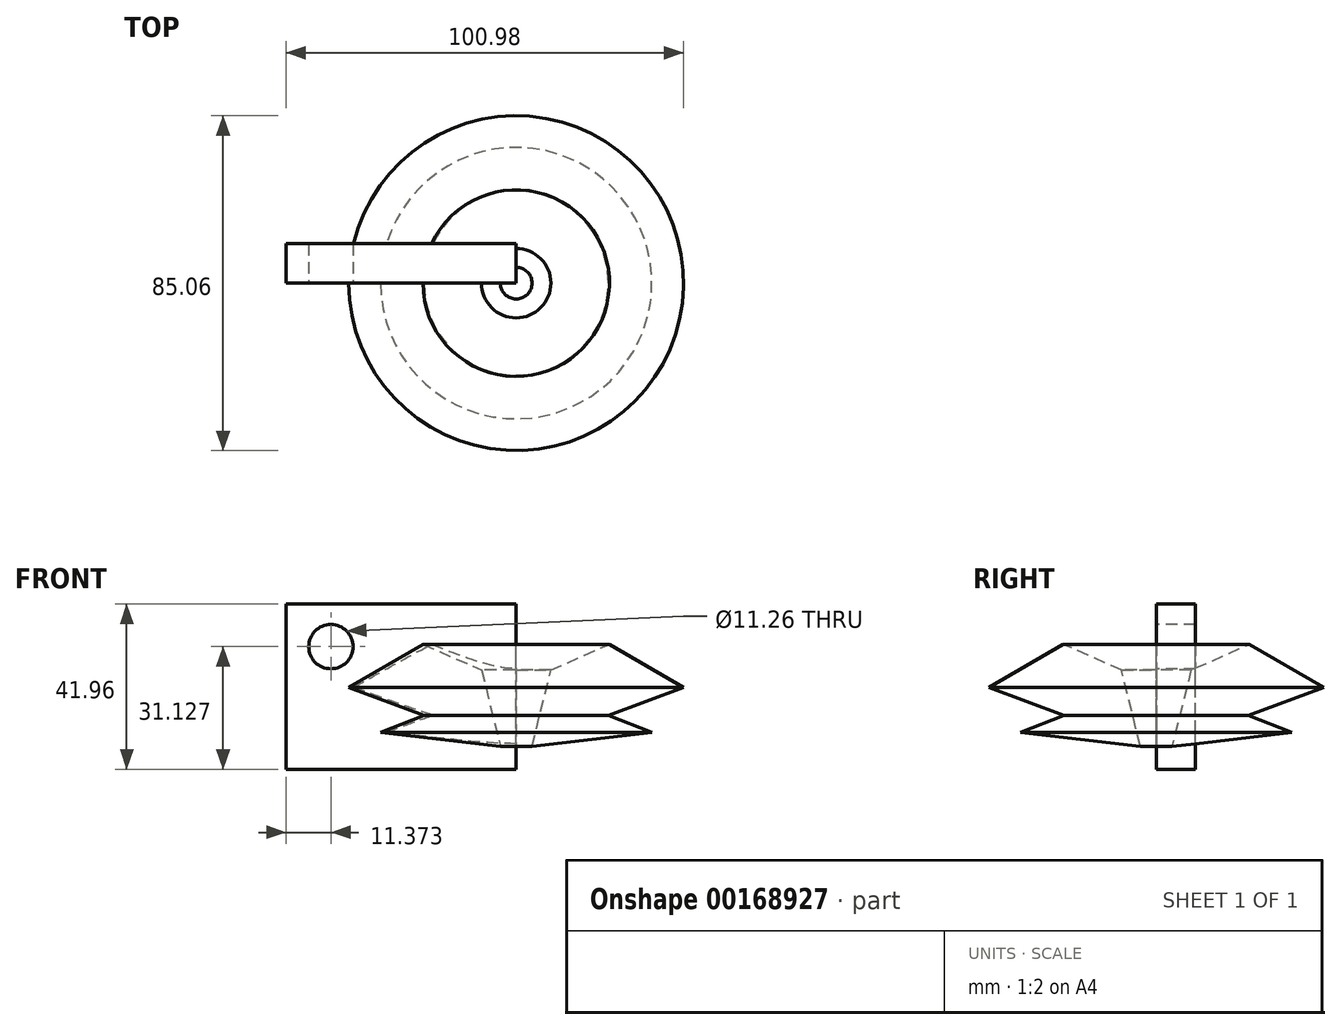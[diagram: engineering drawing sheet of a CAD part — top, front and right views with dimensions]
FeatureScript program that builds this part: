
annotation { "Feature Type Name" : "Feature", "Feature Type Description" : "" }
export const myFeature = defineFeature(function(context is Context, id is Id, definition is map)
    precondition{}
    {
        {
            var Q0;
            Q0=qCreatedBy(makeId("Front.planeOp"),FACE);
            var sketch = newSketch(context, id + "F0", { "sketchPlane" : qUnion([Q0])});
            skLineSegment(sketch, "E0.bottom", {"start": v(0, 0) * mm, "end": v(58.45, 0) * mm});
            skLineSegment(sketch, "E0.top", {"start": v(0, 41.96) * mm, "end": v(58.45, 41.96) * mm});
            skLineSegment(sketch, "E0.left", {"start": v(0, 0) * mm, "end": v(0, 41.96) * mm});
            skLineSegment(sketch, "E0.right", {"start": v(58.45, 0) * mm, "end": v(58.45, 41.96) * mm});
            skSolve(sketch);
        }
        {
            var Q0;
            Q0=makeQuery(id+"F0.imprint","IMPRINT",FACE,{"disambiguationData":[TD([[makeQuery(id+"F0.imprint","IMPRINT",EDGE,{"derivedFrom":sQuery(id+"F0.wireOp",EDGE,"E0.bottom")}),1.0]])]});
            extrude(context, id + "F1", {"entities" : qUnion([Q0]), "depth" : 10 * mm, "offsetDistance" : 25.4 * mm});
        }
        {
            var Q0;
            Q0=makeQuery(id+"F1.opExtrude","CAP_FACE",FACE,{"disambiguationData":[OSD([sQuery(id+"F0.wireOp",EDGE,"E0.bottom"),sQuery(id+"F0.wireOp",EDGE,"E0.top"),sQuery(id+"F0.wireOp",EDGE,"E0.left"),sQuery(id+"F0.wireOp",EDGE,"E0.right")])],"isStart":false});
            var sketch = newSketch(context, id + "F2", { "sketchPlane" : qUnion([Q0])});
            skCircle(sketch, "E1", {"center": v(11.37, 31.13) * mm, "radius": 5.63 * mm});
            skSolve(sketch);
        }
        {
            var Q0;
            Q0=makeQuery(id+"F2.imprint","IMPRINT",FACE,{"disambiguationData":[TD([[makeQuery(id+"F2.imprint","IMPRINT",EDGE,{"derivedFrom":sQuery(id+"F2.wireOp",EDGE,"E1")}),1.0]])]});
            extrude(context, id + "F3", {"entities" : qUnion([Q0]), "operationType" : NewBodyOperationType.REMOVE, "endBound" : BoundingType.THROUGH_ALL, "oppositeDirection" : true, "depth" : 25.4 * mm, "offsetDistance" : 25.4 * mm});
        }
        {
            var Q0;
            Q0=makeQuery(id+"F1.opExtrude","CAP_FACE",FACE,{"disambiguationData":[OSD([sQuery(id+"F0.wireOp",EDGE,"E0.bottom"),sQuery(id+"F0.wireOp",EDGE,"E0.top"),sQuery(id+"F0.wireOp",EDGE,"E0.left"),sQuery(id+"F0.wireOp",EDGE,"E0.right")])],"isStart":false});
            var sketch = newSketch(context, id + "F4", { "sketchPlane" : qUnion([Q0])});
            skLineSegment(sketch, "E2", {"start": v(34.76, 31.75) * mm, "end": v(15.93, 20.76) * mm});
            skLineSegment(sketch, "E3", {"start": v(15.93, 20.76) * mm, "end": v(35.03, 13.68) * mm});
            skLineSegment(sketch, "E4", {"start": v(35.03, 13.68) * mm, "end": v(24, 9.38) * mm});
            skLineSegment(sketch, "E5", {"start": v(24, 9.38) * mm, "end": v(54.43, 5.76) * mm});
            skLineSegment(sketch, "E6", {"start": v(54.43, 5.76) * mm, "end": v(49.63, 25.17) * mm});
            skLineSegment(sketch, "E7", {"start": v(49.63, 25.17) * mm, "end": v(34.76, 31.75) * mm});
            skSolve(sketch);
        }
        {
            var Q0;
            Q0=makeQuery(id+"F4.imprint","IMPRINT",FACE,{"disambiguationData":[TD([[makeQuery(id+"F4.imprint","IMPRINT",EDGE,{"derivedFrom":sQuery(id+"F4.wireOp",EDGE,"E2")}),1.0]])]});
            var Q1;
            Q1=makeQuery(id+"F1.opExtrude","CAP_EDGE",EDGE,{"disambiguationData":[OSD([sQuery(id+"F0.wireOp",EDGE,"E0.right")])],"isStart":false});
            revolve(context, id + "F5", {"operationType" : NewBodyOperationType.ADD, "surfaceOperationType" : NewSurfaceOperationType.NEW, "entities" : qUnion([Q0]), "axis" : qUnion([Q1]), "revolveType" : RevolveType.FULL});
        }
    });
